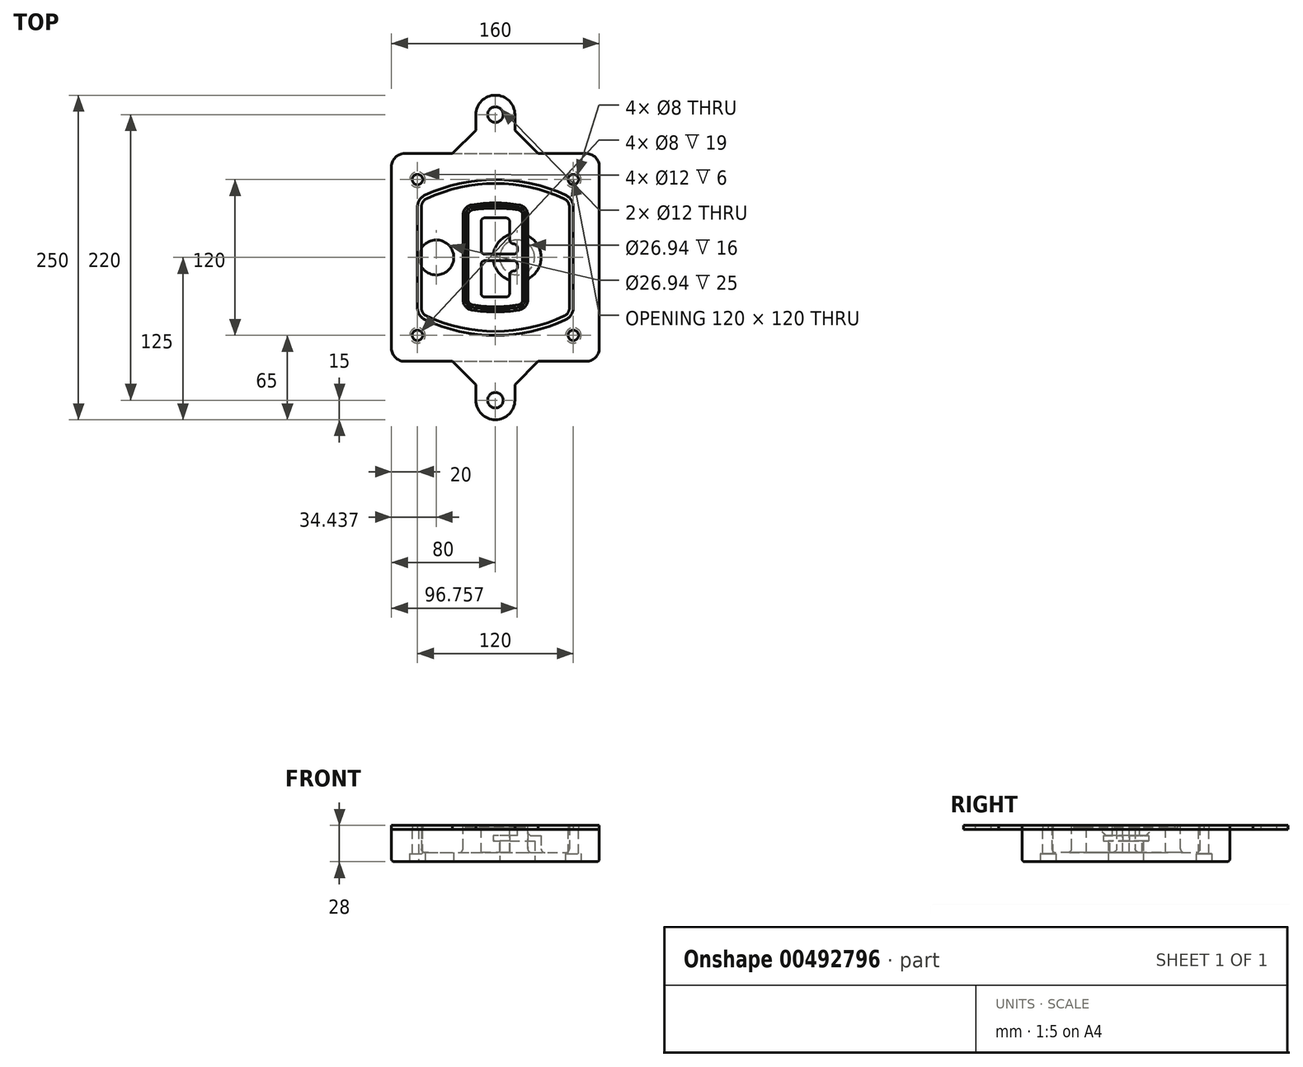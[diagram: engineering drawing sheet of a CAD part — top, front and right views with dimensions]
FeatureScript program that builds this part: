
annotation { "Feature Type Name" : "Feature", "Feature Type Description" : "" }
export const myFeature = defineFeature(function(context is Context, id is Id, definition is map)
    precondition{}
    {
        {
            var Q0;
            Q0=qCreatedBy(makeId("Top.planeOp"),FACE);
            var sketch = newSketch(context, id + "F0", { "sketchPlane" : qUnion([Q0])});
            skPoint(sketch, "E0.rect.middle", {"position": v(0, 0) * mm});
            skLineSegment(sketch, "E1.bottom", {"start": v(-70, -80) * mm, "end": v(70, -80) * mm});
            skLineSegment(sketch, "E1.top", {"start": v(-70, 80) * mm, "end": v(70, 80) * mm});
            skLineSegment(sketch, "E1.left", {"start": v(-80, -70) * mm, "end": v(-80, 70) * mm});
            skLineSegment(sketch, "E1.right", {"start": v(80, -70) * mm, "end": v(80, 70) * mm});
            skLineSegment(sketch, "E2", {"start": v(-80, 80) * mm, "end": v(80, -80) * mm, "construction": true});
            skLineSegment(sketch, "E3", {"start": v(80, 80) * mm, "end": v(-80, -80) * mm, "construction": true});
            skCircle(sketch, "E4", {"center": v(-60, 60) * mm, "radius": 4 * mm});
            skCircle(sketch, "E5", {"center": v(60, 60) * mm, "radius": 4 * mm});
            skCircle(sketch, "E6", {"center": v(60, -60) * mm, "radius": 4 * mm});
            skCircle(sketch, "E7", {"center": v(-60, -60) * mm, "radius": 4 * mm});
            skLineSegment(sketch, "E8", {"start": v(-60, 60) * mm, "end": v(60, 60) * mm, "construction": true});
            skLineSegment(sketch, "E9", {"start": v(60, 60) * mm, "end": v(60, -60) * mm, "construction": true});
            skLineSegment(sketch, "E10", {"start": v(60, -60) * mm, "end": v(-60, -60) * mm, "construction": true});
            skLineSegment(sketch, "E11", {"start": v(-60, -60) * mm, "end": v(-60, 60) * mm, "construction": true});
            skLineSegment(sketch, "E12", {"start": v(-60, 38.83) * mm, "end": v(-60, -38.83) * mm});
            skLineSegment(sketch, "E13", {"start": v(60, 38.83) * mm, "end": v(60, -38.83) * mm});
            skArc(sketch, "E14", {"start": v(54.26, 47.88) * mm, "mid": v(0, 60) * mm, "end": v(-54.26, 47.88) * mm});
            skArc(sketch, "E15", {"start": v(-54.26, -47.88) * mm, "mid": v(0, -60) * mm, "end": v(54.26, -47.88) * mm});
            skLineSegment(sketch, "E16", {"start": v(-60, 0) * mm, "end": v(60, 0) * mm, "construction": true});
            skPoint(sketch, "E17.visualSharp", {"position": v(-60, -45) * mm});
            skArc(sketch, "E17.filletArc", {"start": v(-60, -38.83) * mm, "mid": v(-58.44, -44.2) * mm, "end": v(-54.26, -47.88) * mm});
            skPoint(sketch, "E18.visualSharp", {"position": v(-60, 45) * mm});
            skArc(sketch, "E18.filletArc", {"start": v(-54.26, 47.88) * mm, "mid": v(-58.44, 44.2) * mm, "end": v(-60, 38.83) * mm});
            skPoint(sketch, "E19.visualSharp", {"position": v(60, 45) * mm});
            skArc(sketch, "E19.filletArc", {"start": v(60, 38.83) * mm, "mid": v(58.44, 44.2) * mm, "end": v(54.26, 47.88) * mm});
            skPoint(sketch, "E20.visualSharp", {"position": v(60, -45) * mm});
            skArc(sketch, "E20.filletArc", {"start": v(54.26, -47.88) * mm, "mid": v(58.44, -44.2) * mm, "end": v(60, -38.83) * mm});
            skPoint(sketch, "E21.visualSharp", {"position": v(-80, 80) * mm});
            skArc(sketch, "E21.filletArc", {"start": v(-70, 80) * mm, "mid": v(-77.07, 77.07) * mm, "end": v(-80, 70) * mm});
            skPoint(sketch, "E22.visualSharp", {"position": v(80, 80) * mm});
            skArc(sketch, "E22.filletArc", {"start": v(80, 70) * mm, "mid": v(77.07, 77.07) * mm, "end": v(70, 80) * mm});
            skPoint(sketch, "E23.visualSharp", {"position": v(80, -80) * mm});
            skArc(sketch, "E23.filletArc", {"start": v(70, -80) * mm, "mid": v(77.07, -77.07) * mm, "end": v(80, -70) * mm});
            skPoint(sketch, "E24.visualSharp", {"position": v(-80, -80) * mm});
            skArc(sketch, "E24.filletArc", {"start": v(-80, -70) * mm, "mid": v(-77.07, -77.07) * mm, "end": v(-70, -80) * mm});
            skArc(sketch, "E25.0", {"start": v(57, 38.83) * mm, "mid": v(55.9, 42.58) * mm, "end": v(52.98, 45.17) * mm});
            skLineSegment(sketch, "E25.1", {"start": v(57, 38.83) * mm, "end": v(57, -38.83) * mm});
            skArc(sketch, "E25.2", {"start": v(52.98, -45.17) * mm, "mid": v(55.9, -42.58) * mm, "end": v(57, -38.83) * mm});
            skArc(sketch, "E25.3", {"start": v(-52.98, -45.17) * mm, "mid": v(0, -57) * mm, "end": v(52.98, -45.17) * mm});
            skArc(sketch, "E25.4", {"start": v(-57, -38.83) * mm, "mid": v(-55.9, -42.58) * mm, "end": v(-52.98, -45.17) * mm});
            skArc(sketch, "E25.5", {"start": v(52.98, 45.17) * mm, "mid": v(0, 57) * mm, "end": v(-52.98, 45.17) * mm});
            skLineSegment(sketch, "E25.6", {"start": v(-57, 38.83) * mm, "end": v(-57, -38.83) * mm});
            skArc(sketch, "E25.7", {"start": v(-52.98, 45.17) * mm, "mid": v(-55.9, 42.58) * mm, "end": v(-57, 38.83) * mm});
            skArc(sketch, "E26.0", {"start": v(-55.96, 51.5) * mm, "mid": v(-61.82, 46.33) * mm, "end": v(-64, 38.83) * mm});
            skArc(sketch, "E26.1", {"start": v(55.96, 51.5) * mm, "mid": v(0, 64) * mm, "end": v(-55.96, 51.5) * mm});
            skArc(sketch, "E26.2", {"start": v(64, 38.83) * mm, "mid": v(61.82, 46.33) * mm, "end": v(55.96, 51.5) * mm});
            skLineSegment(sketch, "E26.3", {"start": v(64, 38.83) * mm, "end": v(64, -38.83) * mm});
            skArc(sketch, "E26.4", {"start": v(55.96, -51.5) * mm, "mid": v(61.82, -46.33) * mm, "end": v(64, -38.83) * mm});
            skLineSegment(sketch, "E26.5", {"start": v(-64, 38.83) * mm, "end": v(-64, -38.83) * mm});
            skArc(sketch, "E26.6", {"start": v(-55.96, -51.5) * mm, "mid": v(0, -64) * mm, "end": v(55.96, -51.5) * mm});
            skArc(sketch, "E26.7", {"start": v(-64, -38.83) * mm, "mid": v(-61.82, -46.33) * mm, "end": v(-55.96, -51.5) * mm});
            skSolve(sketch);
        }
        {
            var Q0;
            Q0=makeQuery(id+"F0.imprint","IMPRINT",FACE,{"disambiguationData":[TD([[makeQuery(id+"F0.imprint","IMPRINT",EDGE,{"derivedFrom":sQuery(id+"F0.wireOp",EDGE,"E1.bottom")}),1.0]])]});
            var Q1;
            Q1=makeQuery(id+"F0.imprint","IMPRINT",FACE,{"disambiguationData":[TD([[makeQuery(id+"F0.imprint","IMPRINT",EDGE,{"derivedFrom":sQuery(id+"F0.wireOp",EDGE,"E12")}),1.0]])]});
            var Q2;
            Q2=makeQuery(id+"F0.imprint","IMPRINT",FACE,{"disambiguationData":[TD([[makeQuery(id+"F0.imprint","IMPRINT",EDGE,{"derivedFrom":sQuery(id+"F0.wireOp",EDGE,"E25.0")}),1.0]])]});
            var Q3;
            Q3=makeQuery(id+"F0.imprint","IMPRINT",FACE,{"disambiguationData":[TD([[makeQuery(id+"F0.imprint","IMPRINT",EDGE,{"derivedFrom":sQuery(id+"F0.wireOp",EDGE,"E12")}),-1.0]])]});
            extrude(context, id + "F1", {"entities" : qUnion([Q0, Q1, Q2, Q3]), "oppositeDirection" : true, "depth" : 25 * mm});
        }
        {
            var Q0;
            Q0=makeQuery(id+"F0.imprint","IMPRINT",FACE,{"disambiguationData":[TD([[makeQuery(id+"F0.imprint","IMPRINT",EDGE,{"derivedFrom":sQuery(id+"F0.wireOp",EDGE,"E12")}),1.0]])]});
            extrude(context, id + "F2", {"entities" : qUnion([Q0]), "operationType" : NewBodyOperationType.ADD, "depth" : 3 * mm});
        }
        {
            var Q0;
            Q0=makeQuery(id+"F0.imprint","IMPRINT",FACE,{"disambiguationData":[TD([[makeQuery(id+"F0.imprint","IMPRINT",EDGE,{"derivedFrom":sQuery(id+"F0.wireOp",EDGE,"E25.0")}),1.0]])]});
            extrude(context, id + "F3", {"entities" : qUnion([Q0]), "operationType" : NewBodyOperationType.REMOVE, "oppositeDirection" : true, "depth" : 18 * mm});
        }
        {
            var Q0;
            Q0=makeQuery(id+"F2.opExtrude","CAP_FACE",FACE,{"disambiguationData":[OSD([sQuery(id+"F0.wireOp",EDGE,"E12"),sQuery(id+"F0.wireOp",EDGE,"E13"),sQuery(id+"F0.wireOp",EDGE,"E14"),sQuery(id+"F0.wireOp",EDGE,"E15"),sQuery(id+"F0.wireOp",EDGE,"E17.filletArc"),sQuery(id+"F0.wireOp",EDGE,"E18.filletArc"),sQuery(id+"F0.wireOp",EDGE,"E19.filletArc"),sQuery(id+"F0.wireOp",EDGE,"E20.filletArc"),sQuery(id+"F0.wireOp",EDGE,"E25.0"),sQuery(id+"F0.wireOp",EDGE,"E25.1"),sQuery(id+"F0.wireOp",EDGE,"E25.2"),sQuery(id+"F0.wireOp",EDGE,"E25.3"),sQuery(id+"F0.wireOp",EDGE,"E25.4"),sQuery(id+"F0.wireOp",EDGE,"E25.5"),sQuery(id+"F0.wireOp",EDGE,"E25.6"),sQuery(id+"F0.wireOp",EDGE,"E25.7")])],"isStart":false});
            var sketch = newSketch(context, id + "F4", { "sketchPlane" : qUnion([Q0])});
            skArc(sketch, "E27.0", {"start": v(-18.34, -40.45) * mm, "mid": v(0, -42) * mm, "end": v(18.34, -40.45) * mm});
            skArc(sketch, "E28.0", {"start": v(18.34, 40.45) * mm, "mid": v(0, 42) * mm, "end": v(-18.34, 40.45) * mm});
            skLineSegment(sketch, "E29", {"start": v(-25, 32.57) * mm, "end": v(-25, -32.57) * mm});
            skLineSegment(sketch, "E30", {"start": v(25, 32.57) * mm, "end": v(25, -32.57) * mm});
            skLineSegment(sketch, "E31", {"start": v(-25, 39.1) * mm, "end": v(25, 39.1) * mm, "construction": true});
            skLineSegment(sketch, "E32", {"start": v(-25, -39.1) * mm, "end": v(25, -39.1) * mm, "construction": true});
            skPoint(sketch, "E33.visualSharp", {"position": v(-25, 39.1) * mm});
            skArc(sketch, "E33.filletArc", {"start": v(-18.34, 40.45) * mm, "mid": v(-23.11, 37.73) * mm, "end": v(-25, 32.57) * mm});
            skPoint(sketch, "E34.visualSharp", {"position": v(25, 39.1) * mm});
            skArc(sketch, "E34.filletArc", {"start": v(25, 32.57) * mm, "mid": v(23.11, 37.73) * mm, "end": v(18.34, 40.45) * mm});
            skPoint(sketch, "E35.visualSharp", {"position": v(25, -39.1) * mm});
            skArc(sketch, "E35.filletArc", {"start": v(18.34, -40.45) * mm, "mid": v(23.11, -37.73) * mm, "end": v(25, -32.57) * mm});
            skPoint(sketch, "E36.visualSharp", {"position": v(-25, -39.1) * mm});
            skArc(sketch, "E36.filletArc", {"start": v(-25, -32.57) * mm, "mid": v(-23.11, -37.73) * mm, "end": v(-18.34, -40.45) * mm});
            skArc(sketch, "E37.0", {"start": v(52.98, 45.17) * mm, "mid": v(0, 57) * mm, "end": v(-52.98, 45.17) * mm});
            skArc(sketch, "E37.1", {"start": v(-52.98, 45.17) * mm, "mid": v(-55.9, 42.58) * mm, "end": v(-57, 38.83) * mm});
            skLineSegment(sketch, "E37.2", {"start": v(-57, 38.83) * mm, "end": v(-57, -38.83) * mm});
            skArc(sketch, "E37.3", {"start": v(-57, -38.83) * mm, "mid": v(-55.9, -42.58) * mm, "end": v(-52.98, -45.17) * mm});
            skArc(sketch, "E37.4", {"start": v(-52.98, -45.17) * mm, "mid": v(0, -57) * mm, "end": v(52.98, -45.17) * mm});
            skArc(sketch, "E37.5", {"start": v(52.98, -45.17) * mm, "mid": v(55.9, -42.58) * mm, "end": v(57, -38.83) * mm});
            skLineSegment(sketch, "E37.6", {"start": v(57, 38.83) * mm, "end": v(57, -38.83) * mm});
            skArc(sketch, "E37.7", {"start": v(57, 38.83) * mm, "mid": v(55.9, 42.58) * mm, "end": v(52.98, 45.17) * mm});
            skLineSegment(sketch, "E38.0", {"start": v(23, 32.57) * mm, "end": v(23, -32.57) * mm});
            skArc(sketch, "E38.1", {"start": v(18, -38.48) * mm, "mid": v(21.58, -36.44) * mm, "end": v(23, -32.57) * mm});
            skArc(sketch, "E38.2", {"start": v(-18, -38.48) * mm, "mid": v(0, -40) * mm, "end": v(18, -38.48) * mm});
            skArc(sketch, "E38.3", {"start": v(-23, -32.57) * mm, "mid": v(-21.58, -36.44) * mm, "end": v(-18, -38.48) * mm});
            skLineSegment(sketch, "E38.4", {"start": v(-23, 32.57) * mm, "end": v(-23, -32.57) * mm});
            skArc(sketch, "E38.5", {"start": v(23, 32.57) * mm, "mid": v(21.58, 36.44) * mm, "end": v(18, 38.48) * mm});
            skArc(sketch, "E38.6", {"start": v(-18, 38.48) * mm, "mid": v(-21.58, 36.44) * mm, "end": v(-23, 32.57) * mm});
            skArc(sketch, "E38.7", {"start": v(18, 38.48) * mm, "mid": v(0, 40) * mm, "end": v(-18, 38.48) * mm});
            skArc(sketch, "E39.0", {"start": v(21, 32.57) * mm, "mid": v(20.06, 35.15) * mm, "end": v(17.67, 36.5) * mm});
            skLineSegment(sketch, "E39.1", {"start": v(21, 32.57) * mm, "end": v(21, -32.57) * mm});
            skArc(sketch, "E39.2", {"start": v(17.67, -36.5) * mm, "mid": v(20.06, -35.15) * mm, "end": v(21, -32.57) * mm});
            skArc(sketch, "E39.3", {"start": v(-17.67, -36.5) * mm, "mid": v(0, -38) * mm, "end": v(17.67, -36.5) * mm});
            skArc(sketch, "E39.4", {"start": v(-21, -32.57) * mm, "mid": v(-20.06, -35.15) * mm, "end": v(-17.67, -36.5) * mm});
            skArc(sketch, "E39.5", {"start": v(17.67, 36.5) * mm, "mid": v(0, 38) * mm, "end": v(-17.67, 36.5) * mm});
            skLineSegment(sketch, "E39.6", {"start": v(-21, 32.57) * mm, "end": v(-21, -32.57) * mm});
            skArc(sketch, "E39.7", {"start": v(-17.67, 36.5) * mm, "mid": v(-20.06, 35.15) * mm, "end": v(-21, 32.57) * mm});
            skLineSegment(sketch, "E40", {"start": v(-25, 0) * mm, "end": v(25, 0) * mm, "construction": true});
            skLineSegment(sketch, "E41", {"start": v(-11, 5.5) * mm, "end": v(-11, 27.5) * mm});
            skLineSegment(sketch, "E42", {"start": v(-8, 30.5) * mm, "end": v(8, 30.5) * mm});
            skLineSegment(sketch, "E43", {"start": v(11, 27.5) * mm, "end": v(11, 13.5) * mm});
            skLineSegment(sketch, "E44", {"start": v(14, 10.5) * mm, "end": v(14, 10.5) * mm});
            skLineSegment(sketch, "E45", {"start": v(17, 7.5) * mm, "end": v(17, 5.5) * mm});
            skLineSegment(sketch, "E46", {"start": v(14, 2.5) * mm, "end": v(-8, 2.5) * mm});
            skPoint(sketch, "E47.visualSharp", {"position": v(-11, 30.5) * mm});
            skArc(sketch, "E47.filletArc", {"start": v(-8, 30.5) * mm, "mid": v(-10.12, 29.62) * mm, "end": v(-11, 27.5) * mm});
            skPoint(sketch, "E48.visualSharp", {"position": v(11, 30.5) * mm});
            skArc(sketch, "E48.filletArc", {"start": v(11, 27.5) * mm, "mid": v(10.12, 29.62) * mm, "end": v(8, 30.5) * mm});
            skPoint(sketch, "E49.visualSharp", {"position": v(11, 10.5) * mm});
            skArc(sketch, "E49.filletArc", {"start": v(11, 13.5) * mm, "mid": v(11.88, 11.38) * mm, "end": v(14, 10.5) * mm});
            skPoint(sketch, "E50.visualSharp", {"position": v(17, 10.5) * mm});
            skArc(sketch, "E50.filletArc", {"start": v(17, 7.5) * mm, "mid": v(16.12, 9.62) * mm, "end": v(14, 10.5) * mm});
            skPoint(sketch, "E51.visualSharp", {"position": v(17, 2.5) * mm});
            skArc(sketch, "E51.filletArc", {"start": v(14, 2.5) * mm, "mid": v(16.12, 3.38) * mm, "end": v(17, 5.5) * mm});
            skPoint(sketch, "E52.visualSharp", {"position": v(-11, 2.5) * mm});
            skArc(sketch, "E52.filletArc", {"start": v(-11, 5.5) * mm, "mid": v(-10.12, 3.38) * mm, "end": v(-8, 2.5) * mm});
            skLineSegment(sketch, "E53.0.MirrorCS", {"start": v(14, -2.5) * mm, "end": v(-8, -2.5) * mm});
            skArc(sketch, "E54.0.MirrorCS", {"start": v(-11, -5.5) * mm, "mid": v(-10.12, -3.38) * mm, "end": v(-8, -2.5) * mm});
            skLineSegment(sketch, "E55.0.MirrorCS", {"start": v(-11, -5.5) * mm, "end": v(-11, -27.5) * mm});
            skArc(sketch, "E56.0.MirrorCS", {"start": v(-8, -30.5) * mm, "mid": v(-10.12, -29.62) * mm, "end": v(-11, -27.5) * mm});
            skLineSegment(sketch, "E57.0.MirrorCS", {"start": v(-8, -30.5) * mm, "end": v(8, -30.5) * mm});
            skArc(sketch, "E58.0.MirrorCS", {"start": v(11, -27.5) * mm, "mid": v(10.12, -29.62) * mm, "end": v(8, -30.5) * mm});
            skLineSegment(sketch, "E59.0.MirrorCS", {"start": v(11, -27.5) * mm, "end": v(11, -13.5) * mm});
            skArc(sketch, "E60.0.MirrorCS", {"start": v(11, -13.5) * mm, "mid": v(11.88, -11.38) * mm, "end": v(14, -10.5) * mm});
            skArc(sketch, "E61.0.MirrorCS", {"start": v(17, -7.5) * mm, "mid": v(16.12, -9.62) * mm, "end": v(14, -10.5) * mm});
            skLineSegment(sketch, "E62.0.MirrorCS", {"start": v(17, -7.5) * mm, "end": v(17, -5.5) * mm});
            skArc(sketch, "E63.0.MirrorCS", {"start": v(14, -2.5) * mm, "mid": v(16.12, -3.38) * mm, "end": v(17, -5.5) * mm});
            skSolve(sketch);
        }
        {
            var Q0;
            Q0=makeQuery(id+"F4.imprint","IMPRINT",FACE,{"disambiguationData":[TD([[makeQuery(id+"F4.imprint","IMPRINT",EDGE,{"derivedFrom":sQuery(id+"F4.wireOp",EDGE,"E27.0")}),1.0]])]});
            var Q1;
            Q1=makeQuery(id+"F4.imprint","IMPRINT",FACE,{"disambiguationData":[TD([[makeQuery(id+"F4.imprint","IMPRINT",EDGE,{"derivedFrom":sQuery(id+"F4.wireOp",EDGE,"E38.0")}),-1.0]])]});
            var Q2;
            Q2=makeQuery(id+"F4.imprint","IMPRINT",FACE,{"disambiguationData":[TD([[makeQuery(id+"F4.imprint","IMPRINT",EDGE,{"derivedFrom":sQuery(id+"F4.wireOp",EDGE,"E39.0")}),1.0]])]});
            extrude(context, id + "F5", {"entities" : qUnion([Q0, Q1, Q2]), "operationType" : NewBodyOperationType.ADD, "endBound" : BoundingType.UP_TO_NEXT, "oppositeDirection" : true, "depth" : 25 * mm});
        }
        {
            var Q0;
            Q0=makeQuery(id+"F4.imprint","IMPRINT",FACE,{"disambiguationData":[TD([[makeQuery(id+"F4.imprint","IMPRINT",EDGE,{"derivedFrom":sQuery(id+"F4.wireOp",EDGE,"E38.0")}),-1.0]])]});
            extrude(context, id + "F6", {"entities" : qUnion([Q0]), "operationType" : NewBodyOperationType.REMOVE, "oppositeDirection" : true, "depth" : 2 * mm});
        }
        {
            var Q0;
            Q0=makeQuery(id+"F1.opExtrude","CAP_FACE",FACE,{"disambiguationData":[OSD([sQuery(id+"F0.wireOp",EDGE,"E1.bottom"),sQuery(id+"F0.wireOp",EDGE,"E1.top"),sQuery(id+"F0.wireOp",EDGE,"E1.left"),sQuery(id+"F0.wireOp",EDGE,"E1.right"),sQuery(id+"F0.wireOp",EDGE,"E4"),sQuery(id+"F0.wireOp",EDGE,"E5"),sQuery(id+"F0.wireOp",EDGE,"E6"),sQuery(id+"F0.wireOp",EDGE,"E7"),sQuery(id+"F0.wireOp",EDGE,"E21.filletArc"),sQuery(id+"F0.wireOp",EDGE,"E22.filletArc"),sQuery(id+"F0.wireOp",EDGE,"E23.filletArc"),sQuery(id+"F0.wireOp",EDGE,"E24.filletArc")])],"isStart":false});
            var sketch = newSketch(context, id + "F7", { "sketchPlane" : qUnion([Q0])});
            skCircle(sketch, "E64", {"center": v(16.76, 0) * mm, "radius": 13.47 * mm});
            skCircle(sketch, "E65", {"center": v(-45.56, 0) * mm, "radius": 13.47 * mm});
            skLineSegment(sketch, "E66", {"start": v(80, 0) * mm, "end": v(-80, 0) * mm});
            skCircle(sketch, "E67", {"center": v(16.76, 0) * mm, "radius": 18.47 * mm});
            skCircle(sketch, "E68", {"center": v(60, -60) * mm, "radius": 6 * mm});
            skCircle(sketch, "E69", {"center": v(-60, -60) * mm, "radius": 6 * mm});
            skCircle(sketch, "E70", {"center": v(-60, 60) * mm, "radius": 6 * mm});
            skCircle(sketch, "E71", {"center": v(60, 60) * mm, "radius": 6 * mm});
            skSolve(sketch);
        }
        {
            var Q0;
            {var subQ1=sQuery(id+"F7.wireOp",EDGE,"E66");var subQ4=sQuery(id+"F7.wireOp",EDGE,"E64");var subQ6=makeQuery(id+"F7.imprint","INTERSECT",VERTEX,{"disambiguationData":[OD(0.0)],"derivedFrom":[subQ4,subQ1]});Q0=makeQuery(id+"F7.imprint","IMPRINT",FACE,{"disambiguationData":[TD([[makeQuery(id+"F7.imprint","IMPRINT",EDGE,{"disambiguationData":[TD([[subQ6,-1.0]])],"derivedFrom":subQ4}),-1.0]])]});}
            var Q1;
            {var subQ0=sQuery(id+"F7.wireOp",EDGE,"E66");var subQ1=sQuery(id+"F7.wireOp",EDGE,"E64");var subQ3=makeQuery(id+"F7.imprint","INTERSECT",VERTEX,{"disambiguationData":[OD(0.0)],"derivedFrom":[subQ1,subQ0]});Q1=makeQuery(id+"F7.imprint","IMPRINT",FACE,{"disambiguationData":[TD([[makeQuery(id+"F7.imprint","IMPRINT",EDGE,{"disambiguationData":[TD([[subQ3,-1.0]])],"derivedFrom":subQ1}),1.0]])]});}
            var Q2;
            {var subQ0=sQuery(id+"F7.wireOp",EDGE,"E66");var subQ1=sQuery(id+"F7.wireOp",EDGE,"E64");var subQ3=makeQuery(id+"F7.imprint","INTERSECT",VERTEX,{"disambiguationData":[OD(0.0)],"derivedFrom":[subQ1,subQ0]});Q2=makeQuery(id+"F7.imprint","IMPRINT",FACE,{"disambiguationData":[TD([[makeQuery(id+"F7.imprint","IMPRINT",EDGE,{"disambiguationData":[TD([[subQ3,1.0]])],"derivedFrom":subQ1}),1.0]])]});}
            var Q3;
            {var subQ1=sQuery(id+"F7.wireOp",EDGE,"E66");var subQ4=sQuery(id+"F7.wireOp",EDGE,"E64");var subQ6=makeQuery(id+"F7.imprint","INTERSECT",VERTEX,{"disambiguationData":[OD(0.0)],"derivedFrom":[subQ4,subQ1]});Q3=makeQuery(id+"F7.imprint","IMPRINT",FACE,{"disambiguationData":[TD([[makeQuery(id+"F7.imprint","IMPRINT",EDGE,{"disambiguationData":[TD([[subQ6,1.0]])],"derivedFrom":subQ4}),-1.0]])]});}
            extrude(context, id + "F8", {"entities" : qUnion([Q0, Q1, Q2, Q3]), "operationType" : NewBodyOperationType.ADD, "oppositeDirection" : true, "depth" : 20 * mm});
        }
        {
            var Q0;
            {var subQ0=sQuery(id+"F7.wireOp",EDGE,"E66");var subQ1=sQuery(id+"F7.wireOp",EDGE,"E64");var subQ3=makeQuery(id+"F7.imprint","INTERSECT",VERTEX,{"disambiguationData":[OD(0.0)],"derivedFrom":[subQ1,subQ0]});Q0=makeQuery(id+"F7.imprint","IMPRINT",FACE,{"disambiguationData":[TD([[makeQuery(id+"F7.imprint","IMPRINT",EDGE,{"disambiguationData":[TD([[subQ3,-1.0]])],"derivedFrom":subQ1}),1.0]])]});}
            var Q1;
            {var subQ0=sQuery(id+"F7.wireOp",EDGE,"E66");var subQ1=sQuery(id+"F7.wireOp",EDGE,"E64");var subQ3=makeQuery(id+"F7.imprint","INTERSECT",VERTEX,{"disambiguationData":[OD(0.0)],"derivedFrom":[subQ1,subQ0]});Q1=makeQuery(id+"F7.imprint","IMPRINT",FACE,{"disambiguationData":[TD([[makeQuery(id+"F7.imprint","IMPRINT",EDGE,{"disambiguationData":[TD([[subQ3,1.0]])],"derivedFrom":subQ1}),1.0]])]});}
            extrude(context, id + "F9", {"entities" : qUnion([Q0, Q1]), "operationType" : NewBodyOperationType.REMOVE, "oppositeDirection" : true, "depth" : 16 * mm});
        }
        {
            var Q0;
            {var subQ0=sQuery(id+"F7.wireOp",EDGE,"E66");var subQ1=sQuery(id+"F7.wireOp",EDGE,"E65");var subQ3=makeQuery(id+"F7.imprint","INTERSECT",VERTEX,{"disambiguationData":[OD(0.0)],"derivedFrom":[subQ1,subQ0]});Q0=makeQuery(id+"F7.imprint","IMPRINT",FACE,{"disambiguationData":[TD([[makeQuery(id+"F7.imprint","IMPRINT",EDGE,{"disambiguationData":[TD([[subQ3,-1.0]])],"derivedFrom":subQ1}),1.0]])]});}
            var Q1;
            {var subQ0=sQuery(id+"F7.wireOp",EDGE,"E66");var subQ1=sQuery(id+"F7.wireOp",EDGE,"E65");var subQ3=makeQuery(id+"F7.imprint","INTERSECT",VERTEX,{"disambiguationData":[OD(0.0)],"derivedFrom":[subQ1,subQ0]});Q1=makeQuery(id+"F7.imprint","IMPRINT",FACE,{"disambiguationData":[TD([[makeQuery(id+"F7.imprint","IMPRINT",EDGE,{"disambiguationData":[TD([[subQ3,1.0]])],"derivedFrom":subQ1}),1.0]])]});}
            extrude(context, id + "F10", {"entities" : qUnion([Q0, Q1]), "operationType" : NewBodyOperationType.REMOVE, "oppositeDirection" : true, "depth" : 25 * mm});
        }
        {
            var Q0;
            Q0=makeQuery(id+"F7.imprint","IMPRINT",FACE,{"disambiguationData":[TD([[makeQuery(id+"F7.imprint","IMPRINT",EDGE,{"derivedFrom":sQuery(id+"F7.wireOp",EDGE,"E68")}),1.0]])]});
            var Q1;
            Q1=makeQuery(id+"F7.imprint","IMPRINT",FACE,{"disambiguationData":[TD([[makeQuery(id+"F7.imprint","IMPRINT",EDGE,{"derivedFrom":makeQuery(id+"F1.opExtrude","CAP_EDGE",EDGE,{"disambiguationData":[OSD([sQuery(id+"F0.wireOp",EDGE,"E5")])],"isStart":false})}),-1.0]])]});
            var Q2;
            Q2=makeQuery(id+"F7.imprint","IMPRINT",FACE,{"disambiguationData":[TD([[makeQuery(id+"F7.imprint","IMPRINT",EDGE,{"derivedFrom":sQuery(id+"F7.wireOp",EDGE,"E69")}),1.0]])]});
            var Q3;
            Q3=makeQuery(id+"F7.imprint","IMPRINT",FACE,{"disambiguationData":[TD([[makeQuery(id+"F7.imprint","IMPRINT",EDGE,{"derivedFrom":makeQuery(id+"F1.opExtrude","CAP_EDGE",EDGE,{"disambiguationData":[OSD([sQuery(id+"F0.wireOp",EDGE,"E4")])],"isStart":false})}),-1.0]])]});
            var Q4;
            Q4=makeQuery(id+"F7.imprint","IMPRINT",FACE,{"disambiguationData":[TD([[makeQuery(id+"F7.imprint","IMPRINT",EDGE,{"derivedFrom":sQuery(id+"F7.wireOp",EDGE,"E70")}),1.0]])]});
            var Q5;
            Q5=makeQuery(id+"F7.imprint","IMPRINT",FACE,{"disambiguationData":[TD([[makeQuery(id+"F7.imprint","IMPRINT",EDGE,{"derivedFrom":makeQuery(id+"F1.opExtrude","CAP_EDGE",EDGE,{"disambiguationData":[OSD([sQuery(id+"F0.wireOp",EDGE,"E7")])],"isStart":false})}),-1.0]])]});
            var Q6;
            Q6=makeQuery(id+"F7.imprint","IMPRINT",FACE,{"disambiguationData":[TD([[makeQuery(id+"F7.imprint","IMPRINT",EDGE,{"derivedFrom":sQuery(id+"F7.wireOp",EDGE,"E71")}),1.0]])]});
            var Q7;
            Q7=makeQuery(id+"F7.imprint","IMPRINT",FACE,{"disambiguationData":[TD([[makeQuery(id+"F7.imprint","IMPRINT",EDGE,{"derivedFrom":makeQuery(id+"F1.opExtrude","CAP_EDGE",EDGE,{"disambiguationData":[OSD([sQuery(id+"F0.wireOp",EDGE,"E6")])],"isStart":false})}),-1.0]])]});
            extrude(context, id + "F11", {"entities" : qUnion([Q0, Q1, Q2, Q3, Q4, Q5, Q6, Q7]), "operationType" : NewBodyOperationType.REMOVE, "oppositeDirection" : true, "depth" : 6 * mm});
        }
        {
            var Q0;
            Q0=makeQuery(id+"F9.boolean.opBoolean","COPY",FACE,{"derivedFrom":makeQuery(id+"F9.opExtrude","CAP_FACE",FACE,{"disambiguationData":[OSD([sQuery(id+"F7.wireOp",EDGE,"E64")])],"isStart":false})});
            var sketch = newSketch(context, id + "F12", { "sketchPlane" : qUnion([Q0])});
            skArc(sketch, "E72.0", {"start": v(11, 17.55) * mm, "mid": v(2.57, 11.82) * mm, "end": v(-1.54, 2.5) * mm});
            skArc(sketch, "E72.1", {"start": v(-1.54, -2.5) * mm, "mid": v(2.57, -11.82) * mm, "end": v(11, -17.55) * mm});
            skLineSegment(sketch, "E73", {"start": v(-1.54, -2.5) * mm, "end": v(14, -2.5) * mm});
            skLineSegment(sketch, "E74.0", {"start": v(14, 2.5) * mm, "end": v(-1.54, 2.5) * mm});
            skArc(sketch, "E74.1", {"start": v(14, 2.5) * mm, "mid": v(16.12, 3.38) * mm, "end": v(17, 5.5) * mm});
            skLineSegment(sketch, "E74.2", {"start": v(17, 7.5) * mm, "end": v(17, 5.5) * mm});
            skArc(sketch, "E74.3", {"start": v(17, 7.5) * mm, "mid": v(16.12, 9.62) * mm, "end": v(14, 10.5) * mm});
            skArc(sketch, "E74.4", {"start": v(11, 13.5) * mm, "mid": v(11.88, 11.38) * mm, "end": v(14, 10.5) * mm});
            skLineSegment(sketch, "E74.5", {"start": v(11, 17.55) * mm, "end": v(11, 13.5) * mm});
            skLineSegment(sketch, "E74.7", {"start": v(14, -2.5) * mm, "end": v(-1.54, -2.5) * mm});
            skArc(sketch, "E74.8", {"start": v(14, -2.5) * mm, "mid": v(16.12, -3.38) * mm, "end": v(17, -5.5) * mm});
            skLineSegment(sketch, "E74.9", {"start": v(17, -7.5) * mm, "end": v(17, -5.5) * mm});
            skArc(sketch, "E74.10", {"start": v(17, -7.5) * mm, "mid": v(16.12, -9.62) * mm, "end": v(14, -10.5) * mm});
            skArc(sketch, "E74.11", {"start": v(11, -13.5) * mm, "mid": v(11.88, -11.38) * mm, "end": v(14, -10.5) * mm});
            skLineSegment(sketch, "E74.12", {"start": v(11, -17.55) * mm, "end": v(11, -13.5) * mm});
            skPoint(sketch, "E75.orphan", {"position": v(11, -27.5) * mm});
            skPoint(sketch, "E76.orphan", {"position": v(-8, -2.5) * mm});
            skPoint(sketch, "E77.orphan", {"position": v(-8, 2.5) * mm});
            skPoint(sketch, "E78.orphan", {"position": v(11, 27.5) * mm});
            skSolve(sketch);
        }
        {
            var Q0;
            {var subQ7=sQuery(id+"F12.wireOp",EDGE,"E72.0");var subQ14=sQuery(id+"F12.wireOp",EDGE,"E72.1");var subQ16=sQuery(id+"F12.wireOp",EDGE,"E74.1");var subQ18=sQuery(id+"F12.wireOp",EDGE,"E74.8");Q0=qUnion([makeQuery(id+"F12.imprint","IMPRINT",FACE,{"disambiguationData":[TD([[makeQuery(id+"F12.imprint","IMPRINT",EDGE,{"derivedFrom":subQ7}),1.0]])]}),makeQuery(id+"F12.imprint","IMPRINT",FACE,{"disambiguationData":[TD([[makeQuery(id+"F12.imprint","IMPRINT",EDGE,{"derivedFrom":subQ14}),1.0]])]}),makeQuery(id+"F12.imprint","IMPRINT",FACE,{"disambiguationData":[TD([[makeQuery(id+"F12.imprint","IMPRINT",EDGE,{"derivedFrom":subQ16}),1.0]])]}),makeQuery(id+"F12.imprint","IMPRINT",FACE,{"disambiguationData":[TD([[makeQuery(id+"F12.imprint","IMPRINT",EDGE,{"derivedFrom":subQ18}),-1.0]])]})]);}
            var Q1;
            Q1=makeQuery(id+"F5.boolean.opBoolean","SPLIT",FACE,{"disambiguationData":[TD([makeQuery(id+"F5.opExtrude","SWEPT_FACE",FACE,{"disambiguationData":[OSD([sQuery(id+"F4.wireOp",EDGE,"E41")])]})])],"derivedFrom":makeQuery(id+"F3.boolean.opBoolean","COPY",FACE,{"derivedFrom":makeQuery(id+"F3.opExtrude","CAP_FACE",FACE,{"disambiguationData":[OSD([sQuery(id+"F0.wireOp",EDGE,"E25.0"),sQuery(id+"F0.wireOp",EDGE,"E25.1"),sQuery(id+"F0.wireOp",EDGE,"E25.2"),sQuery(id+"F0.wireOp",EDGE,"E25.3"),sQuery(id+"F0.wireOp",EDGE,"E25.4"),sQuery(id+"F0.wireOp",EDGE,"E25.5"),sQuery(id+"F0.wireOp",EDGE,"E25.6"),sQuery(id+"F0.wireOp",EDGE,"E25.7")])],"isStart":false})})});
            extrude(context, id + "F13", {"entities" : qUnion([Q0]), "operationType" : NewBodyOperationType.REMOVE, "endBound" : BoundingType.UP_TO_SURFACE, "endBoundEntityFace" : qUnion([Q1]), "depth" : 25 * mm});
        }
        {
            var Q0;
            Q0=makeQuery(id+"F3.boolean.opBoolean","COPY",EDGE,{"derivedFrom":makeQuery(id+"F3.opExtrude","CAP_EDGE",EDGE,{"disambiguationData":[OSD([sQuery(id+"F0.wireOp",EDGE,"E25.6")])],"isStart":false})});
            var Q1;
            Q1=makeQuery(id+"F8.boolean.opBoolean","INTERSECT",EDGE,{"derivedFrom":[makeQuery(id+"F5.opExtrude","SWEPT_FACE",FACE,{"disambiguationData":[OSD([sQuery(id+"F4.wireOp",EDGE,"E30")])]}),makeQuery(id+"F8.opExtrude","CAP_FACE",FACE,{"disambiguationData":[OSD([sQuery(id+"F7.wireOp",EDGE,"E67")])],"isStart":false})]});
            var Q2;
            Q2=makeQuery(id+"F8.boolean.opBoolean","INTERSECT",EDGE,{"disambiguationData":[OD(1.0)],"derivedFrom":[makeQuery(id+"F5.opExtrude","SWEPT_FACE",FACE,{"disambiguationData":[OSD([sQuery(id+"F4.wireOp",EDGE,"E30")])]}),makeQuery(id+"F8.opExtrude","SWEPT_FACE",FACE,{"disambiguationData":[OSD([sQuery(id+"F7.wireOp",EDGE,"E67")])]})]});
            var Q3;
            {var subQ0=sQuery(id+"F4.wireOp",EDGE,"E30");Q3=makeQuery(id+"F8.boolean.opBoolean","SPLIT",EDGE,{"disambiguationData":[TD([makeQuery(id+"F5.opExtrude","SWEPT_FACE",FACE,{"disambiguationData":[OSD([sQuery(id+"F4.wireOp",EDGE,"E35.filletArc")])]})])],"derivedFrom":makeQuery(id+"F5.opExtrude","CAP_EDGE",EDGE,{"disambiguationData":[OSD([subQ0])],"isStart":false})});}
            var Q4;
            {var subQ0=sQuery(id+"F0.wireOp",EDGE,"E25.7");var subQ1=sQuery(id+"F0.wireOp",EDGE,"E25.1");var subQ2=sQuery(id+"F0.wireOp",EDGE,"E25.6");var subQ3=sQuery(id+"F0.wireOp",EDGE,"E25.5");var subQ4=sQuery(id+"F0.wireOp",EDGE,"E25.4");var subQ5=sQuery(id+"F0.wireOp",EDGE,"E25.0");var subQ6=sQuery(id+"F0.wireOp",EDGE,"E25.2");var subQ7=sQuery(id+"F0.wireOp",EDGE,"E25.3");Q4=makeQuery(id+"F8.boolean.opBoolean","INTERSECT",EDGE,{"derivedFrom":[makeQuery(id+"F5.boolean.opBoolean","SPLIT",FACE,{"disambiguationData":[TD([makeQuery(id+"F2.opExtrude","SWEPT_FACE",FACE,{"disambiguationData":[OSD([subQ5])]})])],"derivedFrom":makeQuery(id+"F3.boolean.opBoolean","COPY",FACE,{"derivedFrom":makeQuery(id+"F3.opExtrude","CAP_FACE",FACE,{"disambiguationData":[OSD([subQ5,subQ1,subQ6,subQ7,subQ4,subQ3,subQ2,subQ0])],"isStart":false})})}),makeQuery(id+"F8.opExtrude","SWEPT_FACE",FACE,{"disambiguationData":[OSD([sQuery(id+"F7.wireOp",EDGE,"E67")])]})]});}
            var Q5;
            Q5=makeQuery(id+"F8.boolean.opBoolean","INTERSECT",EDGE,{"disambiguationData":[OD(0.0)],"derivedFrom":[makeQuery(id+"F5.opExtrude","SWEPT_FACE",FACE,{"disambiguationData":[OSD([sQuery(id+"F4.wireOp",EDGE,"E30")])]}),makeQuery(id+"F8.opExtrude","SWEPT_FACE",FACE,{"disambiguationData":[OSD([sQuery(id+"F7.wireOp",EDGE,"E67")])]})]});
            fillet(context, id + "F14", {"entities" : qUnion([Q0, Q1, Q2, Q3, Q4, Q5]), "radius" : 3 * mm, "tangentPropagation" : true, "allowEdgeOverflow" : false});
        }
        {
            var Q0;
            Q0=makeQuery(id+"F1.opExtrude","CAP_EDGE",EDGE,{"disambiguationData":[OSD([sQuery(id+"F0.wireOp",EDGE,"E1.bottom")])],"isStart":false});
            fillet(context, id + "F15", {"entities" : qUnion([Q0]), "radius" : 2 * mm, "tangentPropagation" : true, "allowEdgeOverflow" : false});
        }
        {
            var Q0;
            {var subQ0=sQuery(id+"F0.wireOp",EDGE,"E21.filletArc");var subQ1=sQuery(id+"F0.wireOp",EDGE,"E7");var subQ2=sQuery(id+"F0.wireOp",EDGE,"E6");var subQ3=sQuery(id+"F0.wireOp",EDGE,"E5");var subQ4=sQuery(id+"F0.wireOp",EDGE,"E4");var subQ5=sQuery(id+"F0.wireOp",EDGE,"E22.filletArc");var subQ6=sQuery(id+"F0.wireOp",EDGE,"E1.bottom");var subQ7=sQuery(id+"F0.wireOp",EDGE,"E1.right");var subQ8=sQuery(id+"F0.wireOp",EDGE,"E1.top");var subQ9=sQuery(id+"F0.wireOp",EDGE,"E1.left");var subQ10=sQuery(id+"F0.wireOp",EDGE,"E23.filletArc");var subQ11=sQuery(id+"F0.wireOp",EDGE,"E24.filletArc");Q0=makeQuery(id+"F2.boolean.opBoolean","SPLIT",FACE,{"disambiguationData":[TD([makeQuery(id+"F1.opExtrude","SWEPT_FACE",FACE,{"disambiguationData":[OSD([subQ6])]})])],"derivedFrom":makeQuery(id+"F1.opExtrude","CAP_FACE",FACE,{"disambiguationData":[OSD([subQ6,subQ8,subQ9,subQ7,subQ4,subQ3,subQ2,subQ1,subQ0,subQ5,subQ10,subQ11])],"isStart":true})});}
            var sketch = newSketch(context, id + "F16", { "sketchPlane" : qUnion([Q0])});
            skPoint(sketch, "E79.start.orphan", {"position": v(-15, 110) * mm});
            skPoint(sketch, "E80.end.orphan", {"position": v(-15, 98) * mm});
            skLineSegment(sketch, "E81", {"start": v(0, 80) * mm, "end": v(0, 110) * mm, "construction": true});
            skPoint(sketch, "E81.endSnap0", {"position": v(0, 80) * mm});
            skCircle(sketch, "E82", {"center": v(0, 110) * mm, "radius": 6 * mm});
            skLineSegment(sketch, "E83", {"start": v(-33, 80) * mm, "end": v(-15, 98) * mm});
            skLineSegment(sketch, "E84", {"start": v(-15, 98) * mm, "end": v(-15, 110) * mm});
            skLineSegment(sketch, "E85", {"start": v(15, 110) * mm, "end": v(15, 98) * mm});
            skArc(sketch, "E86", {"start": v(15, 110) * mm, "mid": v(0, 125) * mm, "end": v(-15, 110) * mm});
            skLineSegment(sketch, "E87", {"start": v(44.4, 80) * mm, "end": v(-33, 80) * mm});
            skLineSegment(sketch, "E88", {"start": v(15, 98) * mm, "end": v(33, 80) * mm});
            skLineSegment(sketch, "E89", {"start": v(-33, -80) * mm, "end": v(-15, -98) * mm});
            skLineSegment(sketch, "E90", {"start": v(0, -80) * mm, "end": v(0, -110) * mm, "construction": true});
            skCircle(sketch, "E91", {"center": v(0, -110) * mm, "radius": 6 * mm});
            skLineSegment(sketch, "E92", {"start": v(-15, -98) * mm, "end": v(-15, -110) * mm});
            skLineSegment(sketch, "E93", {"start": v(15, -98) * mm, "end": v(15, -110) * mm});
            skArc(sketch, "E94", {"start": v(-15, -110) * mm, "mid": v(0, -125) * mm, "end": v(15, -110) * mm});
            skPoint(sketch, "E95.start.orphan", {"position": v(33, -80) * mm});
            skLineSegment(sketch, "E96", {"start": v(33, -80) * mm, "end": v(15, -98) * mm});
            skSolve(sketch);
        }
        {
            var Q0;
            Q0=makeQuery(id+"F16.imprint","IMPRINT",FACE,{"disambiguationData":[TD([[makeQuery(id+"F16.imprint","IMPRINT",EDGE,{"derivedFrom":sQuery(id+"F16.wireOp",EDGE,"E82")}),-1.0]])]});
            var Q1;
            {var subQ0=sQuery(id+"F16.wireOp",EDGE,"E89");Q1=makeQuery(id+"F16.imprint","IMPRINT",FACE,{"disambiguationData":[TD([[makeQuery(id+"F16.imprint","IMPRINT",EDGE,{"derivedFrom":subQ0}),1.0]])]});}
            var Q2;
            Q2=makeQuery(id+"F16.imprint","IMPRINT",FACE,{"disambiguationData":[TD([[makeQuery(id+"F16.imprint","IMPRINT",EDGE,{"derivedFrom":makeQuery(id+"F1.opExtrude","CAP_EDGE",EDGE,{"disambiguationData":[OSD([sQuery(id+"F0.wireOp",EDGE,"E1.left")])],"isStart":true})}),-1.0]])]});
            var Q3;
            Q3=makeQuery(id+"F2.opExtrude","CAP_FACE",FACE,{"disambiguationData":[OSD([sQuery(id+"F0.wireOp",EDGE,"E12"),sQuery(id+"F0.wireOp",EDGE,"E13"),sQuery(id+"F0.wireOp",EDGE,"E14"),sQuery(id+"F0.wireOp",EDGE,"E15"),sQuery(id+"F0.wireOp",EDGE,"E17.filletArc"),sQuery(id+"F0.wireOp",EDGE,"E18.filletArc"),sQuery(id+"F0.wireOp",EDGE,"E19.filletArc"),sQuery(id+"F0.wireOp",EDGE,"E20.filletArc"),sQuery(id+"F0.wireOp",EDGE,"E25.0"),sQuery(id+"F0.wireOp",EDGE,"E25.1"),sQuery(id+"F0.wireOp",EDGE,"E25.2"),sQuery(id+"F0.wireOp",EDGE,"E25.3"),sQuery(id+"F0.wireOp",EDGE,"E25.4"),sQuery(id+"F0.wireOp",EDGE,"E25.5"),sQuery(id+"F0.wireOp",EDGE,"E25.6"),sQuery(id+"F0.wireOp",EDGE,"E25.7")])],"isStart":false});
            extrude(context, id + "F17", {"entities" : qUnion([Q0, Q1, Q2]), "endBound" : BoundingType.UP_TO_SURFACE, "endBoundEntityFace" : qUnion([Q3]), "depth" : .12 * mm});
        }
    });
